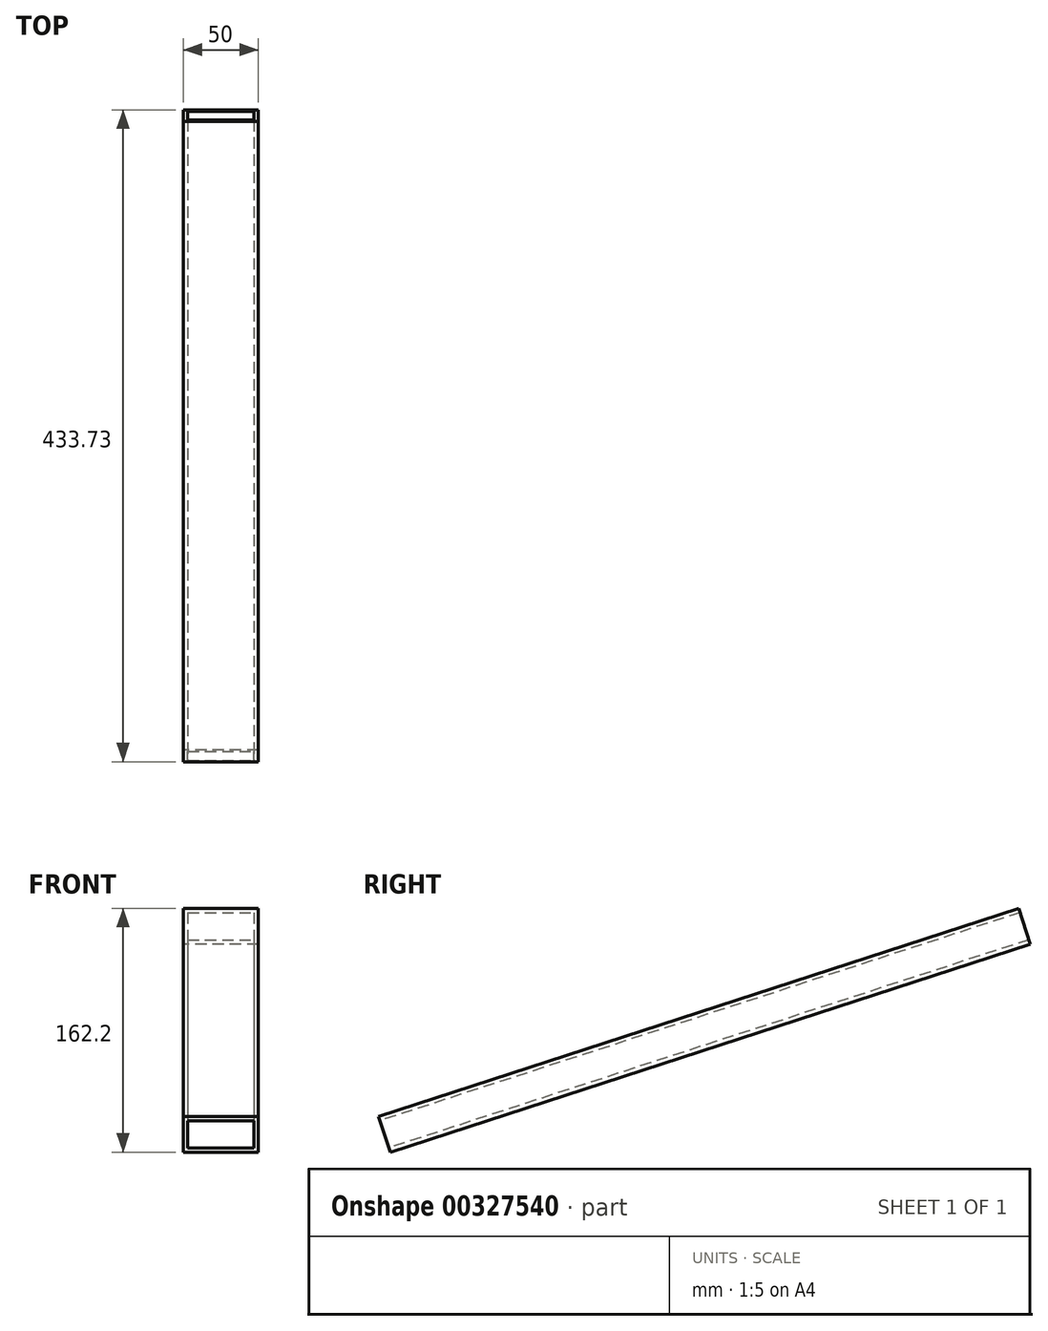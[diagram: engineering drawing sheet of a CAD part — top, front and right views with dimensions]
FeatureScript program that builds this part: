
annotation { "Feature Type Name" : "Feature", "Feature Type Description" : "" }
export const myFeature = defineFeature(function(context is Context, id is Id, definition is map)
    precondition{}
    {
        {
            var Q0;
            Q0=qCreatedBy(makeId("Right.planeOp"),FACE);
            var sketch = newSketch(context, id + "F0", { "sketchPlane" : qUnion([Q0])});
            skLineSegment(sketch, "E0", {"start": v(0, 0) * mm, "end": v(2288, 0) * mm});
            skLineSegment(sketch, "E1", {"start": v(2288, 0) * mm, "end": v(2288, 684.37) * mm});
            skLineSegment(sketch, "E2", {"start": v(2100, 0) * mm, "end": v(2100, 623.29) * mm});
            skLineSegment(sketch, "E3", {"start": v(2050, 0) * mm, "end": v(2050, 607.04) * mm});
            skLineSegment(sketch, "E4", {"start": v(2100, 623.29) * mm, "end": v(2288, 684.37) * mm});
            skLineSegment(sketch, "E5", {"start": v(2100, 623.29) * mm, "end": v(2050, 607.04) * mm});
            skLineSegment(sketch, "E6", {"start": v(2050, 607.04) * mm, "end": v(1862, 545.95) * mm});
            skLineSegment(sketch, "E7", {"start": v(2100, 623.29) * mm, "end": v(2092.27, 647.06) * mm});
            skLineSegment(sketch, "E8", {"start": v(2050, 607.04) * mm, "end": v(2042.27, 630.82) * mm});
            skLineSegment(sketch, "E9", {"start": v(2288, 684.37) * mm, "end": v(2280.27, 708.15) * mm});
            skLineSegment(sketch, "E10", {"start": v(2280.27, 708.15) * mm, "end": v(2092.27, 647.06) * mm});
            skLineSegment(sketch, "E11", {"start": v(2092.27, 647.06) * mm, "end": v(2042.27, 630.82) * mm});
            skLineSegment(sketch, "E12", {"start": v(2042.27, 630.82) * mm, "end": v(1854.27, 569.73) * mm});
            skLineSegment(sketch, "E13", {"start": v(1854.27, 569.73) * mm, "end": v(1862, 545.95) * mm});
            skLineSegment(sketch, "E14", {"start": v(1853.35, 572.58) * mm, "end": v(2279.35, 711) * mm});
            skLineSegment(sketch, "E15", {"start": v(2280.27, 708.15) * mm, "end": v(2279.35, 711) * mm});
            skLineSegment(sketch, "E16", {"start": v(1854.27, 569.73) * mm, "end": v(1853.35, 572.58) * mm});
            skSolve(sketch);
        }
        {
            var Q0;
            {var subQ0=sQuery(id+"F0.wireOp",EDGE,"ijd3VTFd-Imta-bpwi-KAd7-0lDIgMz6j6Lr");var subQ1=sQuery(id+"F0.wireOp",EDGE,"E3");var subQ2=makeQuery(id+"F0.imprint","INTERSECT",VERTEX,{"derivedFrom":[subQ1,subQ0]});Q0=makeQuery(id+"F0.imprint","IMPRINT",FACE,{"disambiguationData":[TD([[makeQuery(id+"F0.imprint","IMPRINT",EDGE,{"disambiguationData":[TD([[subQ2,1.0]])],"derivedFrom":subQ1}),1.0]])]});}
            var Q1;
            Q1=makeQuery(id+"F0.imprint","IMPRINT",FACE,{"disambiguationData":[TD([[makeQuery(id+"F0.imprint","IMPRINT",EDGE,{"derivedFrom":sQuery(id+"F0.wireOp",EDGE,"E6")}),-1.0]])]});
            var Q2;
            Q2=makeQuery(id+"F0.imprint","IMPRINT",FACE,{"disambiguationData":[TD([[makeQuery(id+"F0.imprint","IMPRINT",EDGE,{"derivedFrom":sQuery(id+"F0.wireOp",EDGE,"E5")}),-1.0]])]});
            var Q3;
            Q3=makeQuery(id+"F0.imprint","IMPRINT",FACE,{"disambiguationData":[TD([[makeQuery(id+"F0.imprint","IMPRINT",EDGE,{"derivedFrom":sQuery(id+"F0.wireOp",EDGE,"E4")}),1.0]])]});
            extrude(context, id + "F1", {"entities" : qUnion([Q0, Q1, Q2, Q3]), "depth" : 50 * mm, "symmetric" : true});
        }
        {
            var Q0;
            Q0=makeQuery(id+"F1.opExtrude","SWEPT_FACE",FACE,{"disambiguationData":[OSD([sQuery(id+"F0.wireOp",EDGE,"E13")])]});
            var sketch = newSketch(context, id + "F2", { "sketchPlane" : qUnion([Q0])});
            skLineSegment(sketch, "E17.bottom", {"start": v(-22, -34.16) * mm, "end": v(22, -34.16) * mm});
            skLineSegment(sketch, "E17.top", {"start": v(-22, -53.16) * mm, "end": v(22, -53.16) * mm});
            skLineSegment(sketch, "E17.left", {"start": v(-22, -34.16) * mm, "end": v(-22, -53.16) * mm});
            skLineSegment(sketch, "E17.right", {"start": v(22, -34.16) * mm, "end": v(22, -53.16) * mm});
            skPoint(sketch, "E17.middle", {"position": v(0, -43.66) * mm});
            skPoint(sketch, "E17.middle.positionSnap0", {"position": v(0, -31.16) * mm});
            skPoint(sketch, "E17.middle.positionSnap1", {"position": v(25, -43.66) * mm});
            skPoint(sketch, "E17.centerSnap1", {"position": v(25, -43.66) * mm});
            skSolve(sketch);
        }
        {
            var Q0;
            Q0 = qSketchRegion(id + "F2", true);
            extrude(context, id + "F3", {"entities" : qUnion([Q0]), "operationType" : NewBodyOperationType.REMOVE, "endBound" : BoundingType.THROUGH_ALL, "oppositeDirection" : true, "depth" : 300 * mm});
        }
    });
